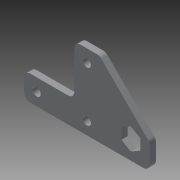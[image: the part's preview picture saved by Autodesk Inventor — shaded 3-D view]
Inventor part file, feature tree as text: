
AUTODESK INVENTOR PART (.ipt)
format: ipt  version: 2014 (Build 180170000, 170)  size: 121,856 bytes
history: native  units: in
note: dims shown in document units (in); Inventor stores cm internally (conversion verified against a paired STEP export)
features: sheet_metal_op x1, fillet x1, sketch x1, other x1
ambient origin geometry x8: Origin, YZ Plane, XZ Plane, XY Plane, X Axis, Y Axis, Z Axis, Center Point
bodies: Solid1 (feature_tree)
feature tree (4):
  sheet_metal_op  "Face1"
  fillet  "Fillet1"  Radius=0.5in
  sketch  "Sketch1"  dims[d1=1.0in d2=1.0in d3=0.5in d4=2.5in d5=0.375in d6=0.375in d7=0.375in d8=90.0deg d9=0.5in d10=0.163in d11=0.25in d12=0.25in d13=0.7874in d15=1.0in d16=0.3937in d18=1.0in d20=0.7874in d22=1.0in d23=0.3937in d25=1.0in d27=0.125in d28=0.125in]
  other  "Plate1"
